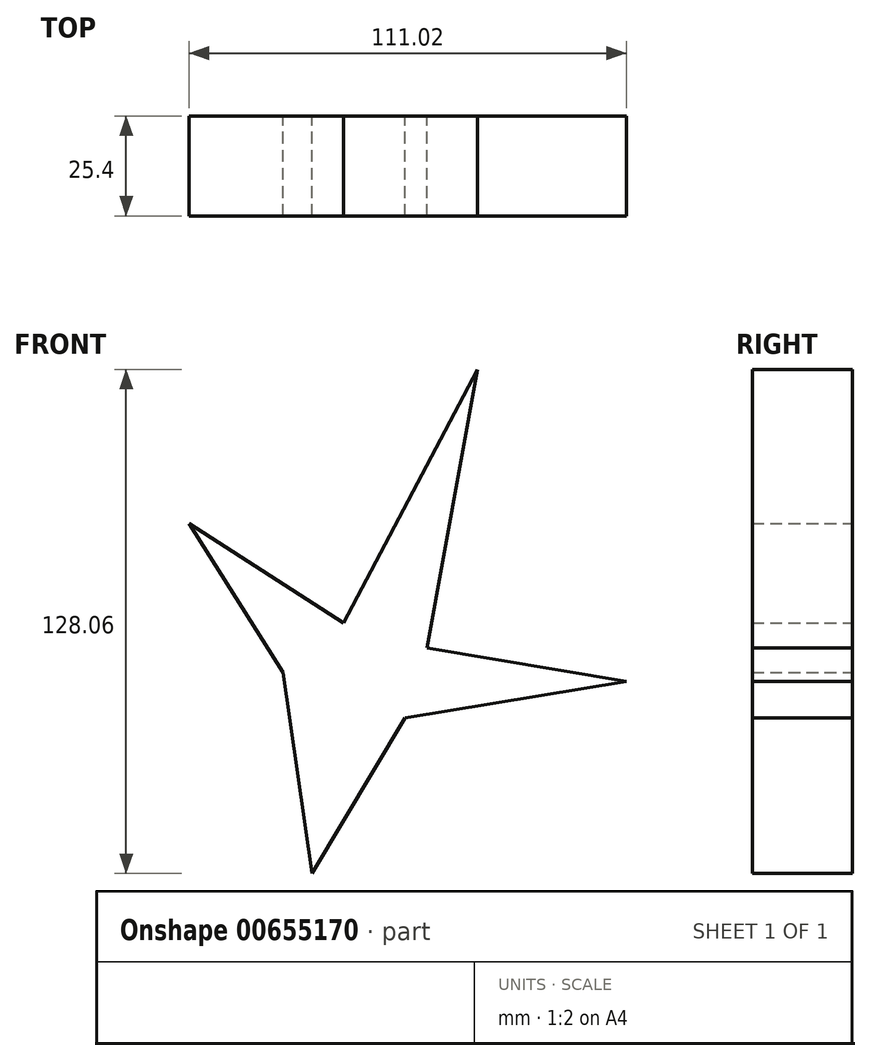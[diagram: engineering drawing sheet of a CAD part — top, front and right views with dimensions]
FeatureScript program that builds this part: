
annotation { "Feature Type Name" : "Feature", "Feature Type Description" : "" }
export const myFeature = defineFeature(function(context is Context, id is Id, definition is map)
    precondition{}
    {
        {
            var Q0;
            Q0=qCreatedBy(makeId("Front.planeOp"),FACE);
            var sketch = newSketch(context, id + "F0", { "sketchPlane" : qUnion([Q0])});
            skLineSegment(sketch, "E0", {"start": v(0, 0) * mm, "end": v(12.92, 70.7) * mm});
            skLineSegment(sketch, "E1", {"start": v(12.92, 70.7) * mm, "end": v(-21.15, 6.25) * mm});
            skLineSegment(sketch, "E2", {"start": v(-21.15, 6.25) * mm, "end": v(-60.34, 31.52) * mm});
            skLineSegment(sketch, "E3", {"start": v(-60.34, 31.52) * mm, "end": v(-36.49, -6.25) * mm});
            skLineSegment(sketch, "E4", {"start": v(-36.49, -6.25) * mm, "end": v(-29.1, -57.36) * mm});
            skLineSegment(sketch, "E5", {"start": v(-29.1, -57.36) * mm, "end": v(-5.54, -17.89) * mm});
            skLineSegment(sketch, "E6", {"start": v(-5.54, -17.89) * mm, "end": v(50.68, -8.52) * mm});
            skLineSegment(sketch, "E7", {"start": v(50.68, -8.52) * mm, "end": v(0, 0) * mm});
            skSolve(sketch);
        }
        {
            var Q0;
            Q0 = qSketchRegion(id + "F0", true);
            extrude(context, id + "F1", {"entities" : qUnion([Q0]), "depth" : 25.4 * mm, "offsetDistance" : 25.4 * mm});
        }
    });
